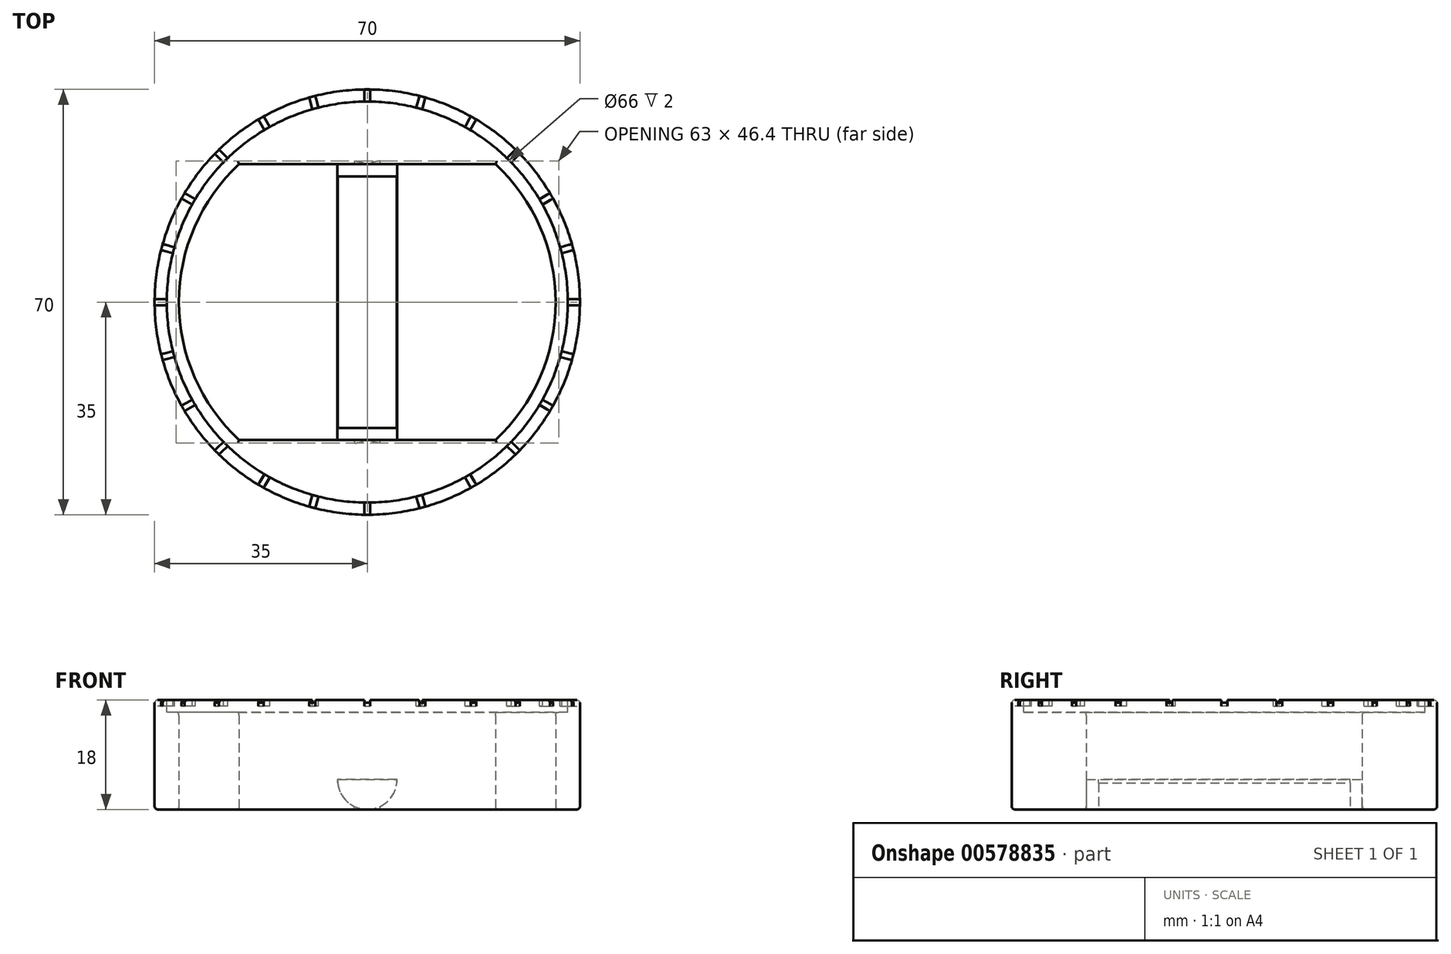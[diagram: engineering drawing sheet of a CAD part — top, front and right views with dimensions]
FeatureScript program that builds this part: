
annotation { "Feature Type Name" : "Feature", "Feature Type Description" : "" }
export const myFeature = defineFeature(function(context is Context, id is Id, definition is map)
    precondition{}
    {
        {
            var Q0;
            Q0=qCreatedBy(makeId("Top.planeOp"),FACE);
            var sketch = newSketch(context, id + "F0", { "sketchPlane" : qUnion([Q0])});
            skCircle(sketch, "E0", {"center": v(0, 0) * mm, "radius": 35 * mm});
            skLineSegment(sketch, "E1", {"start": v(-21.11, -22.7) * mm, "end": v(21.11, -22.7) * mm});
            skLineSegment(sketch, "E2", {"start": v(-21.11, 22.7) * mm, "end": v(21.11, 22.7) * mm});
            skArc(sketch, "E3", {"start": v(-21.11, 22.7) * mm, "mid": v(-31, 0) * mm, "end": v(-21.11, -22.7) * mm});
            skArc(sketch, "E4.trimOffspring", {"start": v(21.11, -22.7) * mm, "mid": v(31, 0) * mm, "end": v(21.11, 22.7) * mm});
            skSolve(sketch);
        }
        {
            var Q0;
            Q0=qSketchRegion(id+"F0",true);
            extrude(context, id + "F1", {"entities" : qUnion([Q0]), "depth" : 18 * mm, "offsetDistance" : 25 * mm});
        }
        {
            var Q0;
            Q0=makeQuery(id+"F1.opExtrude","CAP_FACE",FACE,{"disambiguationData":[OSD([sQuery(id+"F0.wireOp",EDGE,"E0"),sQuery(id+"F0.wireOp",EDGE,"E1"),sQuery(id+"F0.wireOp",EDGE,"E2"),sQuery(id+"F0.wireOp",EDGE,"E3"),sQuery(id+"F0.wireOp",EDGE,"E4.trimOffspring")])],"isStart":false});
            var sketch = newSketch(context, id + "F2", { "sketchPlane" : qUnion([Q0])});
            skCircle(sketch, "E5.0", {"center": v(0, 0) * mm, "radius": 33 * mm});
            skSolve(sketch);
        }
        {
            var Q0;
            Q0=qSketchRegion(id+"F2",true);
            extrude(context, id + "F3", {"entities" : qUnion([Q0]), "operationType" : NewBodyOperationType.REMOVE, "oppositeDirection" : true, "depth" : 2 * mm, "offsetDistance" : 25 * mm});
        }
        {
            var Q0;
            Q0=qCreatedBy(makeId("Front.planeOp"),FACE);
            var sketch = newSketch(context, id + "F4", { "sketchPlane" : qUnion([Q0])});
            skArc(sketch, "E6", {"start": v(-4.9, 4.9) * mm, "mid": v(0, 0) * mm, "end": v(4.9, 4.9) * mm});
            skLineSegment(sketch, "E7", {"start": v(-4.9, 4.9) * mm, "end": v(4.9, 4.9) * mm});
            skSolve(sketch);
        }
        {
            var Q0;
            Q0=qSketchRegion(id+"F4",true);
            var Q1;
            Q1=makeQuery(id+"F1.opExtrude","SWEPT_FACE",FACE,{"disambiguationData":[OSD([sQuery(id+"F0.wireOp",EDGE,"E1")])]});
            var Q2;
            Q2=makeQuery(id+"F1.opExtrude","SWEPT_FACE",FACE,{"disambiguationData":[OSD([sQuery(id+"F0.wireOp",EDGE,"E2")])]});
            extrude(context, id + "F5", {"entities" : qUnion([Q0]), "operationType" : NewBodyOperationType.ADD, "endBound" : BoundingType.UP_TO_SURFACE, "depth" : 25 * mm, "endBoundEntityFace" : qUnion([Q1]), "offsetDistance" : 25 * mm, "hasSecondDirection" : true, "secondDirectionBound" : SecondDirectionBoundingType.UP_TO_SURFACE, "secondDirectionOppositeDirection" : true, "secondDirectionDepth" : 25 * mm, "secondDirectionBoundEntityFace" : qUnion([Q2])});
        }
        {
            var Q0;
            Q0=makeQuery(id+"F3.boolean.opBoolean","COPY",EDGE,{"derivedFrom":makeQuery(id+"F3.opExtrude","CAP_EDGE",EDGE,{"disambiguationData":[OSD([sQuery(id+"F2.wireOp",EDGE,"E5.0")])],"isStart":true})});
            var Q1;
            Q1=makeQuery(id+"F1.opExtrude","CAP_EDGE",EDGE,{"disambiguationData":[OSD([sQuery(id+"F0.wireOp",EDGE,"E0")])],"isStart":false});
            var Q2;
            Q2=makeQuery(id+"F3.boolean.opBoolean","INTERSECT",EDGE,{"derivedFrom":[makeQuery(id+"F1.opExtrude","SWEPT_FACE",FACE,{"disambiguationData":[OSD([sQuery(id+"F0.wireOp",EDGE,"E3")])]}),makeQuery(id+"F3.opExtrude","CAP_FACE",FACE,{"disambiguationData":[OSD([sQuery(id+"F2.wireOp",EDGE,"E5.0")])],"isStart":false})]});
            var Q3;
            Q3=makeQuery(id+"F3.boolean.opBoolean","INTERSECT",EDGE,{"derivedFrom":[makeQuery(id+"F1.opExtrude","SWEPT_FACE",FACE,{"disambiguationData":[OSD([sQuery(id+"F0.wireOp",EDGE,"E4.trimOffspring")])]}),makeQuery(id+"F3.opExtrude","CAP_FACE",FACE,{"disambiguationData":[OSD([sQuery(id+"F2.wireOp",EDGE,"E5.0")])],"isStart":false})]});
            var Q4;
            Q4=makeQuery(id+"F3.boolean.opBoolean","INTERSECT",EDGE,{"derivedFrom":[makeQuery(id+"F1.opExtrude","SWEPT_FACE",FACE,{"disambiguationData":[OSD([sQuery(id+"F0.wireOp",EDGE,"E1")])]}),makeQuery(id+"F3.opExtrude","CAP_FACE",FACE,{"disambiguationData":[OSD([sQuery(id+"F2.wireOp",EDGE,"E5.0")])],"isStart":false})]});
            var Q5;
            Q5=makeQuery(id+"F3.boolean.opBoolean","INTERSECT",EDGE,{"derivedFrom":[makeQuery(id+"F1.opExtrude","SWEPT_FACE",FACE,{"disambiguationData":[OSD([sQuery(id+"F0.wireOp",EDGE,"E2")])]}),makeQuery(id+"F3.opExtrude","CAP_FACE",FACE,{"disambiguationData":[OSD([sQuery(id+"F2.wireOp",EDGE,"E5.0")])],"isStart":false})]});
            var Q6;
            Q6=makeQuery(id+"F5.opExtrude","TWEAK_EDGE",EDGE,{"disambiguationData":[OD(0.0)],"derivedFrom":[makeQuery(id+"F4.imprint","IMPRINT",EDGE,{"derivedFrom":sQuery(id+"F4.wireOp",EDGE,"E6")}),makeQuery(id+"F4.imprint","IMPRINT",EDGE,{"derivedFrom":sQuery(id+"F4.wireOp",EDGE,"E7")})]});
            var Q7;
            Q7=makeQuery(id+"F5.opExtrude","TWEAK_EDGE",EDGE,{"disambiguationData":[OD(1.0)],"derivedFrom":[makeQuery(id+"F4.imprint","IMPRINT",EDGE,{"derivedFrom":sQuery(id+"F4.wireOp",EDGE,"E6")}),makeQuery(id+"F4.imprint","IMPRINT",EDGE,{"derivedFrom":sQuery(id+"F4.wireOp",EDGE,"E7")})]});
            var Q8;
            {var subQ0=sQuery(id+"F0.wireOp",EDGE,"E4.trimOffspring");var subQ1=sQuery(id+"F0.wireOp",EDGE,"E2");Q8=makeQuery(id+"F5.boolean.opBoolean","SPLIT",EDGE,{"disambiguationData":[TD([makeQuery(id+"F1.opExtrude","SWEPT_FACE",FACE,{"disambiguationData":[OSD([subQ0])]})])],"derivedFrom":makeQuery(id+"F1.opExtrude","CAP_EDGE",EDGE,{"disambiguationData":[OSD([subQ1])],"isStart":true})});}
            var Q9;
            {var subQ0=sQuery(id+"F0.wireOp",EDGE,"E3");var subQ1=sQuery(id+"F0.wireOp",EDGE,"E1");Q9=makeQuery(id+"F5.boolean.opBoolean","SPLIT",EDGE,{"disambiguationData":[TD([makeQuery(id+"F1.opExtrude","SWEPT_FACE",FACE,{"disambiguationData":[OSD([subQ0])]})])],"derivedFrom":makeQuery(id+"F1.opExtrude","CAP_EDGE",EDGE,{"disambiguationData":[OSD([subQ1])],"isStart":true})});}
            var Q10;
            Q10=makeQuery(id+"F1.opExtrude","CAP_EDGE",EDGE,{"disambiguationData":[OSD([sQuery(id+"F0.wireOp",EDGE,"E0")])],"isStart":true});
            var Q11;
            Q11=makeQuery(id+"F1.opExtrude","CAP_EDGE",EDGE,{"disambiguationData":[OSD([sQuery(id+"F0.wireOp",EDGE,"E3")])],"isStart":true});
            var Q12;
            Q12=makeQuery(id+"F1.opExtrude","CAP_EDGE",EDGE,{"disambiguationData":[OSD([sQuery(id+"F0.wireOp",EDGE,"E4.trimOffspring")])],"isStart":true});
            fillet(context, id + "F6", {"entities" : qUnion([Q0, Q1, Q2, Q3, Q4, Q5, Q6, Q7, Q8, Q9, Q10, Q11, Q12]), "radius" : 0.5 * mm, "tangentPropagation" : true, "allowEdgeOverflow" : false});
        }
        {
            var Q0;
            Q0=makeQuery(id+"F1.opExtrude","CAP_FACE",FACE,{"disambiguationData":[OSD([sQuery(id+"F0.wireOp",EDGE,"E0"),sQuery(id+"F0.wireOp",EDGE,"E1"),sQuery(id+"F0.wireOp",EDGE,"E2"),sQuery(id+"F0.wireOp",EDGE,"E3"),sQuery(id+"F0.wireOp",EDGE,"E4.trimOffspring")])],"isStart":false});
            var sketch = newSketch(context, id + "F7", { "sketchPlane" : qUnion([Q0])});
            skLineSegment(sketch, "E8.bottom", {"start": v(0.5, 33) * mm, "end": v(-0.5, 33) * mm});
            skLineSegment(sketch, "E8.top", {"start": v(0.5, 35) * mm, "end": v(-0.5, 35) * mm});
            skLineSegment(sketch, "E8.left", {"start": v(0.5, 33) * mm, "end": v(0.5, 35) * mm});
            skLineSegment(sketch, "E8.right", {"start": v(-0.5, 33) * mm, "end": v(-0.5, 35) * mm});
            skPoint(sketch, "E8.middle", {"position": v(0, 34) * mm});
            skLineSegment(sketch, "E9.1.0", {"start": v(9.54, 33.67) * mm, "end": v(8.57, 33.93) * mm});
            skLineSegment(sketch, "E9.1.1", {"start": v(9.02, 31.74) * mm, "end": v(8.06, 32) * mm});
            skPoint(sketch, "E9.1.2", {"position": v(8.8, 32.84) * mm});
            skLineSegment(sketch, "E9.1.3", {"start": v(8.06, 32) * mm, "end": v(8.57, 33.93) * mm});
            skLineSegment(sketch, "E9.1.4", {"start": v(9.02, 31.74) * mm, "end": v(9.54, 33.67) * mm});
            skLineSegment(sketch, "E9.2.0", {"start": v(17.93, 30.06) * mm, "end": v(17.07, 30.56) * mm});
            skLineSegment(sketch, "E9.2.1", {"start": v(16.93, 28.33) * mm, "end": v(16.07, 28.83) * mm});
            skPoint(sketch, "E9.2.2", {"position": v(17, 29.44) * mm});
            skLineSegment(sketch, "E9.2.3", {"start": v(16.07, 28.83) * mm, "end": v(17.07, 30.56) * mm});
            skLineSegment(sketch, "E9.2.4", {"start": v(16.93, 28.33) * mm, "end": v(17.93, 30.06) * mm});
            skLineSegment(sketch, "E9.3.0", {"start": v(25.1, 24.4) * mm, "end": v(24.4, 25.1) * mm});
            skLineSegment(sketch, "E9.3.1", {"start": v(23.69, 22.98) * mm, "end": v(22.98, 23.69) * mm});
            skPoint(sketch, "E9.3.2", {"position": v(24.04, 24.04) * mm});
            skLineSegment(sketch, "E9.3.3", {"start": v(22.98, 23.69) * mm, "end": v(24.4, 25.1) * mm});
            skLineSegment(sketch, "E9.3.4", {"start": v(23.69, 22.98) * mm, "end": v(25.1, 24.4) * mm});
            skLineSegment(sketch, "E9.4.0", {"start": v(30.56, 17.07) * mm, "end": v(30.06, 17.93) * mm});
            skLineSegment(sketch, "E9.4.1", {"start": v(28.83, 16.07) * mm, "end": v(28.33, 16.93) * mm});
            skPoint(sketch, "E9.4.2", {"position": v(29.44, 17) * mm});
            skLineSegment(sketch, "E9.4.3", {"start": v(28.33, 16.93) * mm, "end": v(30.06, 17.93) * mm});
            skLineSegment(sketch, "E9.4.4", {"start": v(28.83, 16.07) * mm, "end": v(30.56, 17.07) * mm});
            skLineSegment(sketch, "E9.5.0", {"start": v(33.93, 8.57) * mm, "end": v(33.67, 9.54) * mm});
            skLineSegment(sketch, "E9.5.1", {"start": v(32, 8.06) * mm, "end": v(31.74, 9.02) * mm});
            skPoint(sketch, "E9.5.2", {"position": v(32.84, 8.8) * mm});
            skLineSegment(sketch, "E9.5.3", {"start": v(31.74, 9.02) * mm, "end": v(33.67, 9.54) * mm});
            skLineSegment(sketch, "E9.5.4", {"start": v(32, 8.06) * mm, "end": v(33.93, 8.57) * mm});
            skLineSegment(sketch, "E9.6.0", {"start": v(35, -0.5) * mm, "end": v(35, 0.5) * mm});
            skLineSegment(sketch, "E9.6.1", {"start": v(33, -0.5) * mm, "end": v(33, 0.5) * mm});
            skPoint(sketch, "E9.6.2", {"position": v(34, 0) * mm});
            skLineSegment(sketch, "E9.6.3", {"start": v(33, 0.5) * mm, "end": v(35, 0.5) * mm});
            skLineSegment(sketch, "E9.6.4", {"start": v(33, -0.5) * mm, "end": v(35, -0.5) * mm});
            skLineSegment(sketch, "E9.7.0", {"start": v(33.67, -9.54) * mm, "end": v(33.93, -8.57) * mm});
            skLineSegment(sketch, "E9.7.1", {"start": v(31.74, -9.02) * mm, "end": v(32, -8.06) * mm});
            skPoint(sketch, "E9.7.2", {"position": v(32.84, -8.8) * mm});
            skLineSegment(sketch, "E9.7.3", {"start": v(32, -8.06) * mm, "end": v(33.93, -8.57) * mm});
            skLineSegment(sketch, "E9.7.4", {"start": v(31.74, -9.02) * mm, "end": v(33.67, -9.54) * mm});
            skLineSegment(sketch, "E9.8.0", {"start": v(30.06, -17.93) * mm, "end": v(30.56, -17.07) * mm});
            skLineSegment(sketch, "E9.8.1", {"start": v(28.33, -16.93) * mm, "end": v(28.83, -16.07) * mm});
            skPoint(sketch, "E9.8.2", {"position": v(29.44, -17) * mm});
            skLineSegment(sketch, "E9.8.3", {"start": v(28.83, -16.07) * mm, "end": v(30.56, -17.07) * mm});
            skLineSegment(sketch, "E9.8.4", {"start": v(28.33, -16.93) * mm, "end": v(30.06, -17.93) * mm});
            skLineSegment(sketch, "E9.9.0", {"start": v(24.4, -25.1) * mm, "end": v(25.1, -24.4) * mm});
            skLineSegment(sketch, "E9.9.1", {"start": v(22.98, -23.69) * mm, "end": v(23.69, -22.98) * mm});
            skPoint(sketch, "E9.9.2", {"position": v(24.04, -24.04) * mm});
            skLineSegment(sketch, "E9.9.3", {"start": v(23.69, -22.98) * mm, "end": v(25.1, -24.4) * mm});
            skLineSegment(sketch, "E9.9.4", {"start": v(22.98, -23.69) * mm, "end": v(24.4, -25.1) * mm});
            skLineSegment(sketch, "E9.10.0", {"start": v(17.07, -30.56) * mm, "end": v(17.93, -30.06) * mm});
            skLineSegment(sketch, "E9.10.1", {"start": v(16.07, -28.83) * mm, "end": v(16.93, -28.33) * mm});
            skPoint(sketch, "E9.10.2", {"position": v(17, -29.44) * mm});
            skLineSegment(sketch, "E9.10.3", {"start": v(16.93, -28.33) * mm, "end": v(17.93, -30.06) * mm});
            skLineSegment(sketch, "E9.10.4", {"start": v(16.07, -28.83) * mm, "end": v(17.07, -30.56) * mm});
            skLineSegment(sketch, "E9.11.0", {"start": v(8.57, -33.93) * mm, "end": v(9.54, -33.67) * mm});
            skLineSegment(sketch, "E9.11.1", {"start": v(8.06, -32) * mm, "end": v(9.02, -31.74) * mm});
            skPoint(sketch, "E9.11.2", {"position": v(8.8, -32.84) * mm});
            skLineSegment(sketch, "E9.11.3", {"start": v(9.02, -31.74) * mm, "end": v(9.54, -33.67) * mm});
            skLineSegment(sketch, "E9.11.4", {"start": v(8.06, -32) * mm, "end": v(8.57, -33.93) * mm});
            skLineSegment(sketch, "E9.12.0", {"start": v(-0.5, -35) * mm, "end": v(0.5, -35) * mm});
            skLineSegment(sketch, "E9.12.1", {"start": v(-0.5, -33) * mm, "end": v(0.5, -33) * mm});
            skPoint(sketch, "E9.12.2", {"position": v(0, -34) * mm});
            skLineSegment(sketch, "E9.12.3", {"start": v(0.5, -33) * mm, "end": v(0.5, -35) * mm});
            skLineSegment(sketch, "E9.12.4", {"start": v(-0.5, -33) * mm, "end": v(-0.5, -35) * mm});
            skLineSegment(sketch, "E9.13.0", {"start": v(-9.54, -33.67) * mm, "end": v(-8.57, -33.93) * mm});
            skLineSegment(sketch, "E9.13.1", {"start": v(-9.02, -31.74) * mm, "end": v(-8.06, -32) * mm});
            skPoint(sketch, "E9.13.2", {"position": v(-8.8, -32.84) * mm});
            skLineSegment(sketch, "E9.13.3", {"start": v(-8.06, -32) * mm, "end": v(-8.57, -33.93) * mm});
            skLineSegment(sketch, "E9.13.4", {"start": v(-9.02, -31.74) * mm, "end": v(-9.54, -33.67) * mm});
            skLineSegment(sketch, "E9.14.0", {"start": v(-17.93, -30.06) * mm, "end": v(-17.07, -30.56) * mm});
            skLineSegment(sketch, "E9.14.1", {"start": v(-16.93, -28.33) * mm, "end": v(-16.07, -28.83) * mm});
            skPoint(sketch, "E9.14.2", {"position": v(-17, -29.44) * mm});
            skLineSegment(sketch, "E9.14.3", {"start": v(-16.07, -28.83) * mm, "end": v(-17.07, -30.56) * mm});
            skLineSegment(sketch, "E9.14.4", {"start": v(-16.93, -28.33) * mm, "end": v(-17.93, -30.06) * mm});
            skLineSegment(sketch, "E9.15.0", {"start": v(-25.1, -24.4) * mm, "end": v(-24.4, -25.1) * mm});
            skLineSegment(sketch, "E9.15.1", {"start": v(-23.69, -22.98) * mm, "end": v(-22.98, -23.69) * mm});
            skPoint(sketch, "E9.15.2", {"position": v(-24.04, -24.04) * mm});
            skLineSegment(sketch, "E9.15.3", {"start": v(-22.98, -23.69) * mm, "end": v(-24.4, -25.1) * mm});
            skLineSegment(sketch, "E9.15.4", {"start": v(-23.69, -22.98) * mm, "end": v(-25.1, -24.4) * mm});
            skLineSegment(sketch, "E9.16.0", {"start": v(-30.56, -17.07) * mm, "end": v(-30.06, -17.93) * mm});
            skLineSegment(sketch, "E9.16.1", {"start": v(-28.83, -16.07) * mm, "end": v(-28.33, -16.93) * mm});
            skPoint(sketch, "E9.16.2", {"position": v(-29.44, -17) * mm});
            skLineSegment(sketch, "E9.16.3", {"start": v(-28.33, -16.93) * mm, "end": v(-30.06, -17.93) * mm});
            skLineSegment(sketch, "E9.16.4", {"start": v(-28.83, -16.07) * mm, "end": v(-30.56, -17.07) * mm});
            skPoint(sketch, "E9.center", {"position": v(0, 0) * mm});
            skLineSegment(sketch, "E9.anchor1", {"start": v(0, 0) * mm, "end": v(-0.5, 33) * mm, "construction": true});
            skLineSegment(sketch, "E9.anchor2", {"start": v(0, 0) * mm, "end": v(-0.5, 33) * mm, "construction": true});
            skLineSegment(sketch, "E10.3.17.0", {"start": v(-32, -8.06) * mm, "end": v(-31.74, -9.02) * mm});
            skLineSegment(sketch, "E10.5.17.0", {"start": v(-33.93, -8.57) * mm, "end": v(-33.67, -9.54) * mm});
            skPoint(sketch, "E10.6.17.0", {"position": v(-32.84, -8.8) * mm});
            skLineSegment(sketch, "E10.7.17.0", {"start": v(-31.74, -9.02) * mm, "end": v(-33.67, -9.54) * mm});
            skLineSegment(sketch, "E10.10.17.0", {"start": v(-32, -8.06) * mm, "end": v(-33.93, -8.57) * mm});
            skLineSegment(sketch, "E10.3.18.0", {"start": v(-33, 0.5) * mm, "end": v(-33, -0.5) * mm});
            skLineSegment(sketch, "E10.5.18.0", {"start": v(-35, 0.5) * mm, "end": v(-35, -0.5) * mm});
            skPoint(sketch, "E10.6.18.0", {"position": v(-34, 0) * mm});
            skLineSegment(sketch, "E10.7.18.0", {"start": v(-33, -0.5) * mm, "end": v(-35, -0.5) * mm});
            skLineSegment(sketch, "E10.10.18.0", {"start": v(-33, 0.5) * mm, "end": v(-35, 0.5) * mm});
            skLineSegment(sketch, "E10.3.19.0", {"start": v(-31.74, 9.02) * mm, "end": v(-32, 8.06) * mm});
            skLineSegment(sketch, "E10.5.19.0", {"start": v(-33.67, 9.54) * mm, "end": v(-33.93, 8.57) * mm});
            skPoint(sketch, "E10.6.19.0", {"position": v(-32.84, 8.8) * mm});
            skLineSegment(sketch, "E10.7.19.0", {"start": v(-32, 8.06) * mm, "end": v(-33.93, 8.57) * mm});
            skLineSegment(sketch, "E10.10.19.0", {"start": v(-31.74, 9.02) * mm, "end": v(-33.67, 9.54) * mm});
            skLineSegment(sketch, "E10.3.20.0", {"start": v(-28.33, 16.93) * mm, "end": v(-28.83, 16.07) * mm});
            skLineSegment(sketch, "E10.5.20.0", {"start": v(-30.06, 17.93) * mm, "end": v(-30.56, 17.07) * mm});
            skPoint(sketch, "E10.6.20.0", {"position": v(-29.44, 17) * mm});
            skLineSegment(sketch, "E10.7.20.0", {"start": v(-28.83, 16.07) * mm, "end": v(-30.56, 17.07) * mm});
            skLineSegment(sketch, "E10.10.20.0", {"start": v(-28.33, 16.93) * mm, "end": v(-30.06, 17.93) * mm});
            skLineSegment(sketch, "E10.3.21.0", {"start": v(-22.98, 23.69) * mm, "end": v(-23.69, 22.98) * mm});
            skLineSegment(sketch, "E10.5.21.0", {"start": v(-24.4, 25.1) * mm, "end": v(-25.1, 24.4) * mm});
            skPoint(sketch, "E10.6.21.0", {"position": v(-24.04, 24.04) * mm});
            skLineSegment(sketch, "E10.7.21.0", {"start": v(-23.69, 22.98) * mm, "end": v(-25.1, 24.4) * mm});
            skLineSegment(sketch, "E10.10.21.0", {"start": v(-22.98, 23.69) * mm, "end": v(-24.4, 25.1) * mm});
            skLineSegment(sketch, "E10.3.22.0", {"start": v(-16.07, 28.83) * mm, "end": v(-16.93, 28.33) * mm});
            skLineSegment(sketch, "E10.5.22.0", {"start": v(-17.07, 30.56) * mm, "end": v(-17.93, 30.06) * mm});
            skPoint(sketch, "E10.6.22.0", {"position": v(-17, 29.44) * mm});
            skLineSegment(sketch, "E10.7.22.0", {"start": v(-16.93, 28.33) * mm, "end": v(-17.93, 30.06) * mm});
            skLineSegment(sketch, "E10.10.22.0", {"start": v(-16.07, 28.83) * mm, "end": v(-17.07, 30.56) * mm});
            skLineSegment(sketch, "E11.3.23.0", {"start": v(-8.06, 32) * mm, "end": v(-9.02, 31.74) * mm});
            skLineSegment(sketch, "E11.5.23.0", {"start": v(-8.57, 33.93) * mm, "end": v(-9.54, 33.67) * mm});
            skPoint(sketch, "E11.6.23.0", {"position": v(-8.8, 32.84) * mm});
            skLineSegment(sketch, "E11.7.23.0", {"start": v(-9.02, 31.74) * mm, "end": v(-9.54, 33.67) * mm});
            skLineSegment(sketch, "E11.10.23.0", {"start": v(-8.06, 32) * mm, "end": v(-8.57, 33.93) * mm});
            skSolve(sketch);
        }
        {
            var Q0;
            Q0=qSketchRegion(id+"F7",true);
            extrude(context, id + "F8", {"entities" : qUnion([Q0]), "operationType" : NewBodyOperationType.REMOVE, "oppositeDirection" : true, "depth" : 1 * mm, "offsetDistance" : 25 * mm});
        }
        {
            var Q0;
            Q0=makeQuery(id+"F5.opExtrude","SWEPT_FACE",FACE,{"disambiguationData":[OSD([sQuery(id+"F4.wireOp",EDGE,"E7")])]});
            var sketch = newSketch(context, id + "F9", { "sketchPlane" : qUnion([Q0])});
            skLineSegment(sketch, "E12.bottom", {"start": v(-4.87, 20.7) * mm, "end": v(4.87, 20.7) * mm});
            skLineSegment(sketch, "E12.top", {"start": v(-4.87, -20.7) * mm, "end": v(4.87, -20.7) * mm});
            skLineSegment(sketch, "E12.left", {"start": v(-4.87, 20.7) * mm, "end": v(-4.87, -20.7) * mm});
            skLineSegment(sketch, "E12.right", {"start": v(4.87, 20.7) * mm, "end": v(4.87, -20.7) * mm});
            skPoint(sketch, "E12.middle", {"position": v(0, 0) * mm});
            skSolve(sketch);
        }
        {
            var Q0;
            Q0 = qSketchRegion(id + "F9", true);
            extrude(context, id + "F10", {"entities" : qUnion([Q0]), "operationType" : NewBodyOperationType.REMOVE, "endBound" : BoundingType.THROUGH_ALL, "oppositeDirection" : true, "depth" : 25 * mm, "offsetDistance" : 25 * mm});
        }
    });
